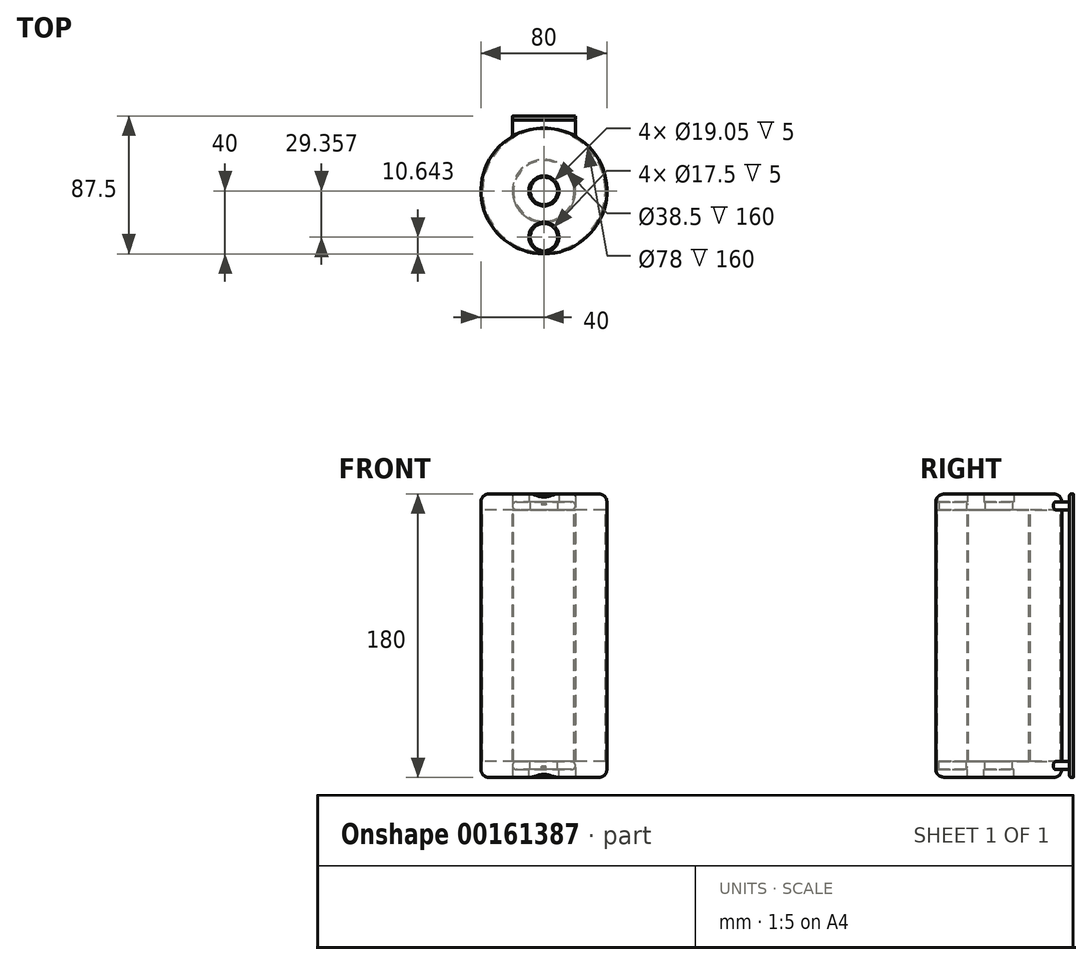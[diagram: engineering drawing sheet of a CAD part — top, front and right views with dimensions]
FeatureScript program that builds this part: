
annotation { "Feature Type Name" : "Feature", "Feature Type Description" : "" }
export const myFeature = defineFeature(function(context is Context, id is Id, definition is map)
    precondition{}
    {
        {
            var Q0;
            Q0=qCreatedBy(makeId("Top.planeOp"),FACE);
            var sketch = newSketch(context, id + "F0", { "sketchPlane" : qUnion([Q0])});
            skCircle(sketch, "E0", {"center": v(0, 0) * mm, "radius": 40 * mm});
            skLineSegment(sketch, "E1", {"start": v(0, 0) * mm, "end": v(0, -20) * mm});
            skLineSegment(sketch, "E2", {"start": v(0, -20) * mm, "end": v(0, -21.21) * mm});
            skLineSegment(sketch, "E3", {"start": v(0, -21.21) * mm, "end": v(0, -37.5) * mm});
            skLineSegment(sketch, "E4", {"start": v(0, -37.5) * mm, "end": v(0, -29.36) * mm});
            skCircle(sketch, "E5", {"center": v(0, -29.36) * mm, "radius": 9.53 * mm});
            skCircle(sketch, "E6", {"center": v(0, 0) * mm, "radius": 9.53 * mm});
            skCircle(sketch, "E7", {"center": v(0, 0) * mm, "radius": 20 * mm});
            skCircle(sketch, "E8", {"center": v(0, 0) * mm, "radius": 19.25 * mm});
            skCircle(sketch, "E9", {"center": v(0, -29.36) * mm, "radius": 8.75 * mm});
            skCircle(sketch, "E10", {"center": v(0, 0) * mm, "radius": 8.75 * mm});
            skCircle(sketch, "E11", {"center": v(0, 0) * mm, "radius": 39 * mm});
            skLineSegment(sketch, "E12.top", {"start": v(20, 40) * mm, "end": v(0, 40) * mm});
            skLineSegment(sketch, "E13.top", {"start": v(0, 40) * mm, "end": v(-20, 40) * mm});
            skLineSegment(sketch, "E14", {"start": v(-20, 34.64) * mm, "end": v(-20, 40) * mm});
            skLineSegment(sketch, "E15", {"start": v(20, 40) * mm, "end": v(20, 34.64) * mm});
            skLineSegment(sketch, "E16.bottom", {"start": v(-20, 40) * mm, "end": v(20, 40) * mm});
            skLineSegment(sketch, "E16.top", {"start": v(-20, 45) * mm, "end": v(20, 45) * mm});
            skLineSegment(sketch, "E16.left", {"start": v(-20, 40) * mm, "end": v(-20, 45) * mm});
            skLineSegment(sketch, "E16.right", {"start": v(20, 40) * mm, "end": v(20, 45) * mm});
            skLineSegment(sketch, "E17.top", {"start": v(-20, 47.5) * mm, "end": v(20, 47.5) * mm});
            skLineSegment(sketch, "E17.left", {"start": v(-20, 45) * mm, "end": v(-20, 47.5) * mm});
            skLineSegment(sketch, "E17.right", {"start": v(20, 45) * mm, "end": v(20, 47.5) * mm});
            skSolve(sketch);
        }
        {
            var Q0;
            Q0=makeQuery(id+"F0.imprint","IMPRINT",FACE,{"disambiguationData":[TD([[makeQuery(id+"F0.imprint","IMPRINT",EDGE,{"derivedFrom":sQuery(id+"F0.wireOp",EDGE,"E11")}),1.0]])]});
            var Q1;
            Q1=makeQuery(id+"F0.imprint","IMPRINT",FACE,{"disambiguationData":[TD([[makeQuery(id+"F0.imprint","IMPRINT",EDGE,{"derivedFrom":sQuery(id+"F0.wireOp",EDGE,"E11")}),-1.0]])]});
            var Q2;
            Q2=makeQuery(id+"F0.imprint","IMPRINT",FACE,{"disambiguationData":[TD([[makeQuery(id+"F0.imprint","IMPRINT",EDGE,{"derivedFrom":sQuery(id+"F0.wireOp",EDGE,"E6")}),1.0]])]});
            var Q3;
            Q3=makeQuery(id+"F0.imprint","IMPRINT",FACE,{"disambiguationData":[TD([[makeQuery(id+"F0.imprint","IMPRINT",EDGE,{"derivedFrom":sQuery(id+"F0.wireOp",EDGE,"E6")}),-1.0]])]});
            var Q4;
            Q4=makeQuery(id+"F0.imprint","IMPRINT",FACE,{"disambiguationData":[TD([[makeQuery(id+"F0.imprint","IMPRINT",EDGE,{"derivedFrom":sQuery(id+"F0.wireOp",EDGE,"E8")}),-1.0]])]});
            var Q5;
            Q5=makeQuery(id+"F0.imprint","IMPRINT",FACE,{"disambiguationData":[TD([[makeQuery(id+"F0.imprint","IMPRINT",EDGE,{"derivedFrom":sQuery(id+"F0.wireOp",EDGE,"E9")}),-1.0]])]});
            extrude(context, id + "F1", {"entities" : qUnion([Q0, Q1, Q2, Q3, Q4, Q5]), "oppositeDirection" : true, "depth" : 10 * mm});
        }
        {
            var Q0;
            Q0 = qSketchRegion(id + "FNYP8afO0flnPvm_4", true);
            var Q1;
            Q1=makeQuery(id+"F0.imprint","IMPRINT",FACE,{"disambiguationData":[TD([[makeQuery(id+"F0.imprint","IMPRINT",EDGE,{"derivedFrom":sQuery(id+"F0.wireOp",EDGE,"E11")}),-1.0]])]});
            var Q2;
            Q2=makeQuery(id+"F0.imprint","IMPRINT",FACE,{"disambiguationData":[TD([[makeQuery(id+"F0.imprint","IMPRINT",EDGE,{"derivedFrom":sQuery(id+"F0.wireOp",EDGE,"E8")}),-1.0]])]});
            extrude(context, id + "F2", {"entities" : qUnion([Q0, Q1, Q2]), "operationType" : NewBodyOperationType.REMOVE, "oppositeDirection" : true, "depth" : 4 * mm});
        }
        {
            var Q0;
            Q0=makeQuery(id+"F0.imprint","IMPRINT",FACE,{"disambiguationData":[TD([[makeQuery(id+"F0.imprint","IMPRINT",EDGE,{"derivedFrom":sQuery(id+"F0.wireOp",EDGE,"E6")}),1.0]])]});
            var Q1;
            {var subQ0=sQuery(id+"F0.wireOp",EDGE,"E7");var subQ1=sQuery(id+"F0.wireOp",EDGE,"E1");var subQ2=makeQuery(id+"F0.imprint","INTERSECT",VERTEX,{"derivedFrom":[subQ1,subQ0]});Q1=makeQuery(id+"F0.imprint","IMPRINT",FACE,{"disambiguationData":[TD([[makeQuery(id+"F0.imprint","IMPRINT",EDGE,{"disambiguationData":[TD([[subQ2,1.0]])],"derivedFrom":subQ1}),1.0]])]});}
            var Q2;
            {var subQ0=sQuery(id+"F0.wireOp",EDGE,"E7");var subQ1=sQuery(id+"F0.wireOp",EDGE,"E1");var subQ2=makeQuery(id+"F0.imprint","INTERSECT",VERTEX,{"derivedFrom":[subQ1,subQ0]});Q2=makeQuery(id+"F0.imprint","IMPRINT",FACE,{"disambiguationData":[TD([[makeQuery(id+"F0.imprint","IMPRINT",EDGE,{"disambiguationData":[TD([[subQ2,1.0]])],"derivedFrom":subQ1}),-1.0]])]});}
            var Q3;
            Q3=makeQuery(id+"F0.imprint","IMPRINT",FACE,{"disambiguationData":[TD([[makeQuery(id+"F0.imprint","IMPRINT",EDGE,{"derivedFrom":sQuery(id+"F0.wireOp",EDGE,"E9")}),-1.0]])]});
            extrude(context, id + "F3", {"entities" : qUnion([Q0, Q1, Q2, Q3]), "operationType" : NewBodyOperationType.REMOVE, "oppositeDirection" : true, "depth" : 10 * mm, "hasSecondDirection" : true, "secondDirectionOppositeDirection" : true, "secondDirectionDepth" : 5 * mm});
        }
        {
            var Q0;
            Q0=makeQuery(id+"F1.opExtrude","CAP_EDGE",EDGE,{"disambiguationData":[OSD([sQuery(id+"F0.wireOp",EDGE,"E0")])],"isStart":false});
            fillet(context, id + "F4", {"entities" : qUnion([Q0]), "radius" : 5 * mm, "tangentPropagation" : true, "allowEdgeOverflow" : false});
        }
        {
            var Q0;
            {var subQ0=sQuery(id+"F0.wireOp",EDGE,"E7");var subQ1=sQuery(id+"F0.wireOp",EDGE,"E1");var subQ2=makeQuery(id+"F0.imprint","INTERSECT",VERTEX,{"derivedFrom":[subQ1,subQ0]});Q0=makeQuery(id+"F0.imprint","IMPRINT",FACE,{"disambiguationData":[TD([[makeQuery(id+"F0.imprint","IMPRINT",EDGE,{"disambiguationData":[TD([[subQ2,1.0]])],"derivedFrom":subQ1}),-1.0]])]});}
            var Q1;
            {var subQ0=sQuery(id+"F0.wireOp",EDGE,"E7");var subQ1=sQuery(id+"F0.wireOp",EDGE,"E1");var subQ2=makeQuery(id+"F0.imprint","INTERSECT",VERTEX,{"derivedFrom":[subQ1,subQ0]});Q1=makeQuery(id+"F0.imprint","IMPRINT",FACE,{"disambiguationData":[TD([[makeQuery(id+"F0.imprint","IMPRINT",EDGE,{"disambiguationData":[TD([[subQ2,1.0]])],"derivedFrom":subQ1}),1.0]])]});}
            extrude(context, id + "F5", {"entities" : qUnion([Q0, Q1]), "operationType" : NewBodyOperationType.ADD, "oppositeDirection" : true, "depth" : 5 * mm, "hasSecondDirection" : true, "secondDirectionOppositeDirection" : true, "secondDirectionDepth" : 4 * mm});
        }
        {
            var Q0;
            Q0=makeQuery(id+"F0.imprint","IMPRINT",FACE,{"disambiguationData":[TD([[makeQuery(id+"F0.imprint","IMPRINT",EDGE,{"derivedFrom":sQuery(id+"F0.wireOp",EDGE,"E11")}),-1.0]])]});
            var Q1;
            Q1=makeQuery(id+"F0.imprint","IMPRINT",FACE,{"disambiguationData":[TD([[makeQuery(id+"F0.imprint","IMPRINT",EDGE,{"derivedFrom":sQuery(id+"F0.wireOp",EDGE,"E8")}),-1.0]])]});
            extrude(context, id + "F6", {"entities" : qUnion([Q0, Q1]), "oppositeDirection" : true, "depth" : 4 * mm, "hasSecondDirection" : true, "secondDirectionOppositeDirection" : true, "secondDirectionDepth" : 3 * mm});
        }
        {
            var Q0;
            Q0=makeQuery(id+"F0.imprint","IMPRINT",FACE,{"disambiguationData":[TD([[makeQuery(id+"F0.imprint","IMPRINT",EDGE,{"derivedFrom":sQuery(id+"F0.wireOp",EDGE,"E11")}),-1.0]])]});
            var Q1;
            Q1=makeQuery(id+"F0.imprint","IMPRINT",FACE,{"disambiguationData":[TD([[makeQuery(id+"F0.imprint","IMPRINT",EDGE,{"derivedFrom":sQuery(id+"F0.wireOp",EDGE,"E8")}),-1.0]])]});
            var Q2;
            {var subQ0=sQuery(id+"F0.wireOp",EDGE,"E7");var subQ1=sQuery(id+"F0.wireOp",EDGE,"E1");var subQ2=makeQuery(id+"F0.imprint","INTERSECT",VERTEX,{"derivedFrom":[subQ1,subQ0]});Q2=makeQuery(id+"F0.imprint","IMPRINT",FACE,{"disambiguationData":[TD([[makeQuery(id+"F0.imprint","IMPRINT",EDGE,{"disambiguationData":[TD([[subQ2,1.0]])],"derivedFrom":subQ1}),1.0]])]});}
            var Q3;
            {var subQ0=sQuery(id+"F0.wireOp",EDGE,"E7");var subQ1=sQuery(id+"F0.wireOp",EDGE,"E1");var subQ2=makeQuery(id+"F0.imprint","INTERSECT",VERTEX,{"derivedFrom":[subQ1,subQ0]});Q3=makeQuery(id+"F0.imprint","IMPRINT",FACE,{"disambiguationData":[TD([[makeQuery(id+"F0.imprint","IMPRINT",EDGE,{"disambiguationData":[TD([[subQ2,1.0]])],"derivedFrom":subQ1}),-1.0]])]});}
            extrude(context, id + "F7", {"entities" : qUnion([Q0, Q1, Q2, Q3]), "depth" : 80 * mm, "hasSecondDirection" : true, "secondDirectionOppositeDirection" : true, "secondDirectionDepth" : 3 * mm});
        }
        {
            var Q0;
            Q0=makeQuery(id+"F7.opExtrude","SWEPT_BODY",BODY,{"disambiguationData":[OSD([sQuery(id+"F0.wireOp",EDGE,"E7"),sQuery(id+"F0.wireOp",EDGE,"E8")])]});
            var Q1;
            Q1=makeQuery(id+"F7.opExtrude","CAP_FACE",FACE,{"disambiguationData":[OSD([sQuery(id+"F0.wireOp",EDGE,"E7"),sQuery(id+"F0.wireOp",EDGE,"E8")])],"isStart":false});
            mirror(context, id + "F8", {"operationType" : NewBodyOperationType.ADD, "entities" : qUnion([Q0]), "mirrorPlane" : qUnion([Q1])});
        }
        {
            var Q0;
            Q0=makeQuery(id+"F1.opExtrude","SWEPT_BODY",BODY,{"disambiguationData":[OSD([sQuery(id+"F0.wireOp",EDGE,"E0"),sQuery(id+"F0.wireOp",EDGE,"E5"),sQuery(id+"F0.wireOp",EDGE,"E7"),sQuery(id+"F0.wireOp",EDGE,"E9"),sQuery(id+"F0.wireOp",EDGE,"E10")])]});
            var Q1;
            Q1=makeQuery(id+"F6.opExtrude","SWEPT_BODY",BODY,{"disambiguationData":[OSD([sQuery(id+"F0.wireOp",EDGE,"E0"),sQuery(id+"F0.wireOp",EDGE,"E11")])]});
            var Q2;
            Q2=makeQuery(id+"F6.opExtrude","SWEPT_BODY",BODY,{"disambiguationData":[OSD([sQuery(id+"F0.wireOp",EDGE,"E5"),sQuery(id+"F0.wireOp",EDGE,"E7"),sQuery(id+"F0.wireOp",EDGE,"E8")])]});
            var Q3;
            Q3=makeQuery(id+"F7.opExtrude","CAP_FACE",FACE,{"disambiguationData":[OSD([sQuery(id+"F0.wireOp",EDGE,"E0"),sQuery(id+"F0.wireOp",EDGE,"E11")])],"isStart":false});
            mirror(context, id + "F9", {"entities" : qUnion([Q0, Q1, Q2]), "mirrorPlane" : qUnion([Q3])});
        }
        {
            var Q0;
            Q0=makeQuery(id+"F7.opExtrude","SWEPT_BODY",BODY,{"disambiguationData":[OSD([sQuery(id+"F0.wireOp",EDGE,"E0"),sQuery(id+"F0.wireOp",EDGE,"E11")])]});
            var Q1;
            Q1=makeQuery(id+"F7.opExtrude","CAP_FACE",FACE,{"disambiguationData":[OSD([sQuery(id+"F0.wireOp",EDGE,"E0"),sQuery(id+"F0.wireOp",EDGE,"E11")])],"isStart":false});
            mirror(context, id + "F10", {"operationType" : NewBodyOperationType.ADD, "entities" : qUnion([Q0]), "mirrorPlane" : qUnion([Q1])});
        }
        {
            var Q0;
            {var subQ0=sQuery(id+"F0.wireOp",EDGE,"E15");Q0=makeQuery(id+"F0.imprint","IMPRINT",FACE,{"disambiguationData":[TD([[makeQuery(id+"F0.imprint","IMPRINT",EDGE,{"derivedFrom":subQ0}),-1.0]])]});}
            var Q1;
            {var subQ0=sQuery(id+"F0.wireOp",EDGE,"E14");Q1=makeQuery(id+"F0.imprint","IMPRINT",FACE,{"disambiguationData":[TD([[makeQuery(id+"F0.imprint","IMPRINT",EDGE,{"derivedFrom":subQ0}),-1.0]])]});}
            var Q2;
            Q2=makeQuery(id+"F0.imprint","IMPRINT",FACE,{"disambiguationData":[TD([[makeQuery(id+"F0.imprint","IMPRINT",EDGE,{"derivedFrom":sQuery(id+"F0.wireOp",EDGE,"E16.top")}),-1.0]])]});
            extrude(context, id + "F11", {"entities" : qUnion([Q0, Q1, Q2]), "depth" : 165 * mm, "hasSecondDirection" : true, "secondDirectionOppositeDirection" : false, "secondDirectionDepth" : 160 * mm});
        }
        {
            var Q0;
            Q0=makeQuery(id+"F1KWkgZxmQ7jtSi_5.opExtrude","CAP_EDGE",EDGE,{"disambiguationData":[OSD([sQuery(id+"F0.wireOp",EDGE,"E14"),sQuery(id+"F0.wireOp",EDGE,"E16.left")])],"isStart":true});
            var Q1;
            Q1=makeQuery(id+"F1KWkgZxmQ7jtSi_5.opExtrude","CAP_EDGE",EDGE,{"disambiguationData":[OSD([sQuery(id+"F0.wireOp",EDGE,"E15"),sQuery(id+"F0.wireOp",EDGE,"E16.right")])],"isStart":true});
            var Q2;
            Q2=makeQuery(id+"F1KWkgZxmQ7jtSi_5.opExtrude","CAP_EDGE",EDGE,{"disambiguationData":[OSD([sQuery(id+"F0.wireOp",EDGE,"E15"),sQuery(id+"F0.wireOp",EDGE,"E16.right")])],"isStart":false});
            var Q3;
            Q3=makeQuery(id+"F1KWkgZxmQ7jtSi_5.opExtrude","CAP_EDGE",EDGE,{"disambiguationData":[OSD([sQuery(id+"F0.wireOp",EDGE,"E14"),sQuery(id+"F0.wireOp",EDGE,"E16.left")])],"isStart":false});
            var Q4;
            Q4=makeQuery(id+"F11.opExtrude","CAP_EDGE",EDGE,{"disambiguationData":[OSD([sQuery(id+"F0.wireOp",EDGE,"E14"),sQuery(id+"F0.wireOp",EDGE,"E16.left")])],"isStart":true});
            var Q5;
            Q5=makeQuery(id+"F11.opExtrude","CAP_EDGE",EDGE,{"disambiguationData":[OSD([sQuery(id+"F0.wireOp",EDGE,"E15"),sQuery(id+"F0.wireOp",EDGE,"E16.right")])],"isStart":true});
            var Q6;
            Q6=makeQuery(id+"F11.opExtrude","CAP_EDGE",EDGE,{"disambiguationData":[OSD([sQuery(id+"F0.wireOp",EDGE,"E15"),sQuery(id+"F0.wireOp",EDGE,"E16.right")])],"isStart":false});
            var Q7;
            Q7=makeQuery(id+"F11.opExtrude","CAP_EDGE",EDGE,{"disambiguationData":[OSD([sQuery(id+"F0.wireOp",EDGE,"E14"),sQuery(id+"F0.wireOp",EDGE,"E16.left")])],"isStart":false});
            fillet(context, id + "F12", {"entities" : qUnion([Q0, Q1, Q2, Q3, Q4, Q5, Q6, Q7]), "radius" : 2.5 * mm, "tangentPropagation" : true, "allowEdgeOverflow" : false});
        }
        {
            var Q0;
            {var subQ1=sQuery(id+"F0.wireOp",EDGE,"E16.left");Q0=makeQuery(id+"F0.imprint","IMPRINT",FACE,{"disambiguationData":[TD([[makeQuery(id+"F0.imprint","IMPRINT",EDGE,{"derivedFrom":subQ1}),-1.0]])]});}
            var Q1;
            {var subQ0=sQuery(id+"F0.wireOp",EDGE,"E14");Q1=makeQuery(id+"F0.imprint","IMPRINT",FACE,{"disambiguationData":[TD([[makeQuery(id+"F0.imprint","IMPRINT",EDGE,{"derivedFrom":subQ0}),-1.0]])]});}
            var Q2;
            {var subQ0=sQuery(id+"F0.wireOp",EDGE,"E15");Q2=makeQuery(id+"F0.imprint","IMPRINT",FACE,{"disambiguationData":[TD([[makeQuery(id+"F0.imprint","IMPRINT",EDGE,{"derivedFrom":subQ0}),-1.0]])]});}
            extrude(context, id + "F13", {"entities" : qUnion([Q0, Q1, Q2]), "operationType" : NewBodyOperationType.ADD, "oppositeDirection" : true, "depth" : 5 * mm});
        }
        {
            var Q0;
            Q0=makeQuery(id+"F13.opExtrude","CAP_EDGE",EDGE,{"disambiguationData":[OSD([sQuery(id+"F0.wireOp",EDGE,"E15"),sQuery(id+"F0.wireOp",EDGE,"E16.right")])],"isStart":false});
            var Q1;
            Q1=makeQuery(id+"F13.opExtrude","CAP_EDGE",EDGE,{"disambiguationData":[OSD([sQuery(id+"F0.wireOp",EDGE,"E15"),sQuery(id+"F0.wireOp",EDGE,"E16.right")])],"isStart":true});
            var Q2;
            Q2=makeQuery(id+"F13.opExtrude","CAP_EDGE",EDGE,{"disambiguationData":[OSD([sQuery(id+"F0.wireOp",EDGE,"E14"),sQuery(id+"F0.wireOp",EDGE,"E16.left")])],"isStart":false});
            var Q3;
            Q3=makeQuery(id+"F13.opExtrude","CAP_EDGE",EDGE,{"disambiguationData":[OSD([sQuery(id+"F0.wireOp",EDGE,"E14"),sQuery(id+"F0.wireOp",EDGE,"E16.left")])],"isStart":true});
            fillet(context, id + "F14", {"entities" : qUnion([Q0, Q1, Q2, Q3]), "radius" : 2.5 * mm, "tangentPropagation" : true, "allowEdgeOverflow" : false});
        }
        {
            var Q0;
            {var subQ1=sQuery(id+"F0.wireOp",EDGE,"E16.left");Q0=makeQuery(id+"F0.imprint","IMPRINT",FACE,{"disambiguationData":[TD([[makeQuery(id+"F0.imprint","IMPRINT",EDGE,{"derivedFrom":subQ1}),-1.0]])]});}
            extrude(context, id + "F15", {"entities" : qUnion([Q0]), "operationType" : NewBodyOperationType.ADD, "depth" : 165 * mm, "hasSecondDirection" : true, "secondDirectionOppositeDirection" : false, "secondDirectionDepth" : 160 * mm});
        }
        {
            var Q0;
            Q0=makeQuery(id+"F15.opExtrude","CAP_EDGE",EDGE,{"disambiguationData":[OSD([sQuery(id+"F0.wireOp",EDGE,"E16.left")])],"isStart":false});
            var Q1;
            Q1=makeQuery(id+"F15.opExtrude","CAP_EDGE",EDGE,{"disambiguationData":[OSD([sQuery(id+"F0.wireOp",EDGE,"E16.left")])],"isStart":true});
            var Q2;
            Q2=makeQuery(id+"F15.opExtrude","CAP_EDGE",EDGE,{"disambiguationData":[OSD([sQuery(id+"F0.wireOp",EDGE,"E16.right")])],"isStart":false});
            var Q3;
            Q3=makeQuery(id+"F15.opExtrude","CAP_EDGE",EDGE,{"disambiguationData":[OSD([sQuery(id+"F0.wireOp",EDGE,"E16.right")])],"isStart":true});
            fillet(context, id + "F16", {"entities" : qUnion([Q0, Q1, Q2, Q3]), "radius" : 2.5 * mm, "tangentPropagation" : true, "allowEdgeOverflow" : false});
        }
        {
            var Q0;
            Q0=makeQuery(id+"F0.imprint","IMPRINT",FACE,{"disambiguationData":[TD([[makeQuery(id+"F0.imprint","IMPRINT",EDGE,{"derivedFrom":sQuery(id+"F0.wireOp",EDGE,"E16.top")}),1.0]])]});
            extrude(context, id + "F17", {"entities" : qUnion([Q0]), "depth" : 170 * mm, "hasSecondDirection" : true, "secondDirectionOppositeDirection" : true, "secondDirectionDepth" : 10 * mm});
        }
        {
            var Q0;
            Q0=makeQuery(id+"F17.opExtrude","SWEPT_EDGE",EDGE,{"disambiguationData":[OSD([sQuery(id+"F0.wireOp",EDGE,"E16.left"),sQuery(id+"F0.wireOp",EDGE,"E16.top"),sQuery(id+"F0.wireOp",EDGE,"E17.left")])]});
            var Q1;
            Q1=makeQuery(id+"F17.opExtrude","CAP_EDGE",EDGE,{"disambiguationData":[OSD([sQuery(id+"F0.wireOp",EDGE,"E16.top")])],"isStart":true});
            var Q2;
            Q2=makeQuery(id+"F17.opExtrude","SWEPT_EDGE",EDGE,{"disambiguationData":[OSD([sQuery(id+"F0.wireOp",EDGE,"E16.right"),sQuery(id+"F0.wireOp",EDGE,"E16.top"),sQuery(id+"F0.wireOp",EDGE,"E17.right")])]});
            var Q3;
            Q3=makeQuery(id+"F17.opExtrude","CAP_EDGE",EDGE,{"disambiguationData":[OSD([sQuery(id+"F0.wireOp",EDGE,"E16.top")])],"isStart":false});
            var Q4;
            Q4=makeQuery(id+"F17.opExtrude","CAP_EDGE",EDGE,{"disambiguationData":[OSD([sQuery(id+"F0.wireOp",EDGE,"E17.right")])],"isStart":false});
            var Q5;
            Q5=makeQuery(id+"F17.opExtrude","CAP_EDGE",EDGE,{"disambiguationData":[OSD([sQuery(id+"F0.wireOp",EDGE,"E17.left")])],"isStart":false});
            var Q6;
            Q6=makeQuery(id+"F17.opExtrude","CAP_EDGE",EDGE,{"disambiguationData":[OSD([sQuery(id+"F0.wireOp",EDGE,"E17.left")])],"isStart":true});
            var Q7;
            Q7=makeQuery(id+"F17.opExtrude","CAP_EDGE",EDGE,{"disambiguationData":[OSD([sQuery(id+"F0.wireOp",EDGE,"E17.right")])],"isStart":true});
            fillet(context, id + "F18", {"entities" : qUnion([Q0, Q1, Q2, Q3, Q4, Q5, Q6, Q7]), "radius" : 1 * mm, "tangentPropagation" : true, "allowEdgeOverflow" : false});
        }
    });
